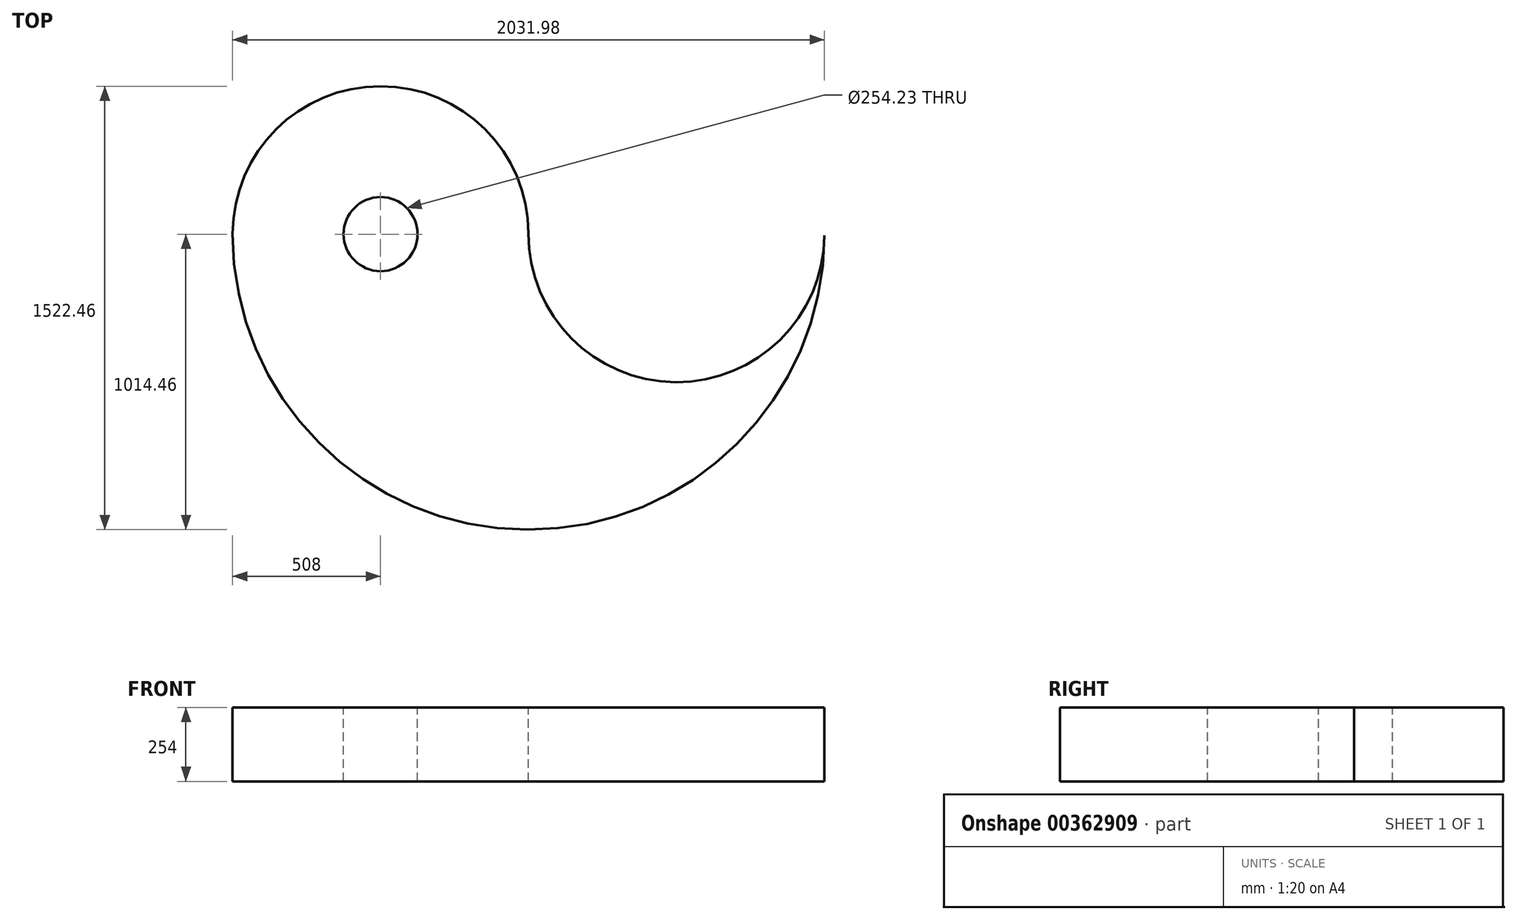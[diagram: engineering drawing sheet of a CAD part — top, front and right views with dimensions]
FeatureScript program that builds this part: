
annotation { "Feature Type Name" : "Feature", "Feature Type Description" : "" }
export const myFeature = defineFeature(function(context is Context, id is Id, definition is map)
    precondition{}
    {
        {
            var Q0;
            Q0=qCreatedBy(makeId("Top.planeOp"),FACE);
            var sketch = newSketch(context, id + "F0", { "sketchPlane" : qUnion([Q0])});
            skCircle(sketch, "E0", {"center": v(0, 0) * mm, "radius": 1016 * mm});
            skSolve(sketch);
        }
        {
            var Q0;
            Q0=makeQuery(id+"F0.imprint","IMPRINT",FACE,{"disambiguationData":[TD([[makeQuery(id+"F0.imprint","IMPRINT",EDGE,{"derivedFrom":sQuery(id+"F0.wireOp",EDGE,"E0")}),1.0]])]});
            extrude(context, id + "F1", {"entities" : qUnion([Q0]), "depth" : 254 * mm});
        }
        {
            var Q0;
            Q0=makeQuery(id+"F1.opExtrude","CAP_FACE",FACE,{"disambiguationData":[OSD([sQuery(id+"F0.wireOp",EDGE,"E0")])],"isStart":false});
            var sketch = newSketch(context, id + "F2", { "sketchPlane" : qUnion([Q0])});
            skArc(sketch, "E1", {"start": v(0, 0) * mm, "mid": v(508, -509.6) * mm, "end": v(1016, 0) * mm});
            skArc(sketch, "E2", {"start": v(0, 0) * mm, "mid": v(-508, 506.46) * mm, "end": v(-1016, 0) * mm});
            skArc(sketch, "E3", {"start": v(1016, 0) * mm, "mid": v(0, 1018.05) * mm, "end": v(-1016, 0) * mm});
            skSolve(sketch);
        }
        {
            var Q0;
            Q0 = qSketchRegion(id + "F2", true);
            extrude(context, id + "F3", {"entities" : qUnion([Q0]), "operationType" : NewBodyOperationType.REMOVE, "endBound" : BoundingType.THROUGH_ALL, "oppositeDirection" : true, "depth" : 25.4 * mm});
        }
        {
            var Q0;
            Q0=makeQuery(id+"F1.opExtrude","CAP_FACE",FACE,{"disambiguationData":[OSD([sQuery(id+"F0.wireOp",EDGE,"E0")])],"isStart":false});
            var sketch = newSketch(context, id + "F4", { "sketchPlane" : qUnion([Q0])});
            skCircle(sketch, "E4", {"center": v(-508, -1.54) * mm, "radius": 127.12 * mm});
            skSolve(sketch);
        }
        {
            var Q0;
            Q0 = qSketchRegion(id + "F4", true);
            extrude(context, id + "F5", {"entities" : qUnion([Q0]), "operationType" : NewBodyOperationType.REMOVE, "endBound" : BoundingType.THROUGH_ALL, "oppositeDirection" : true, "depth" : 25.4 * mm});
        }
    });
